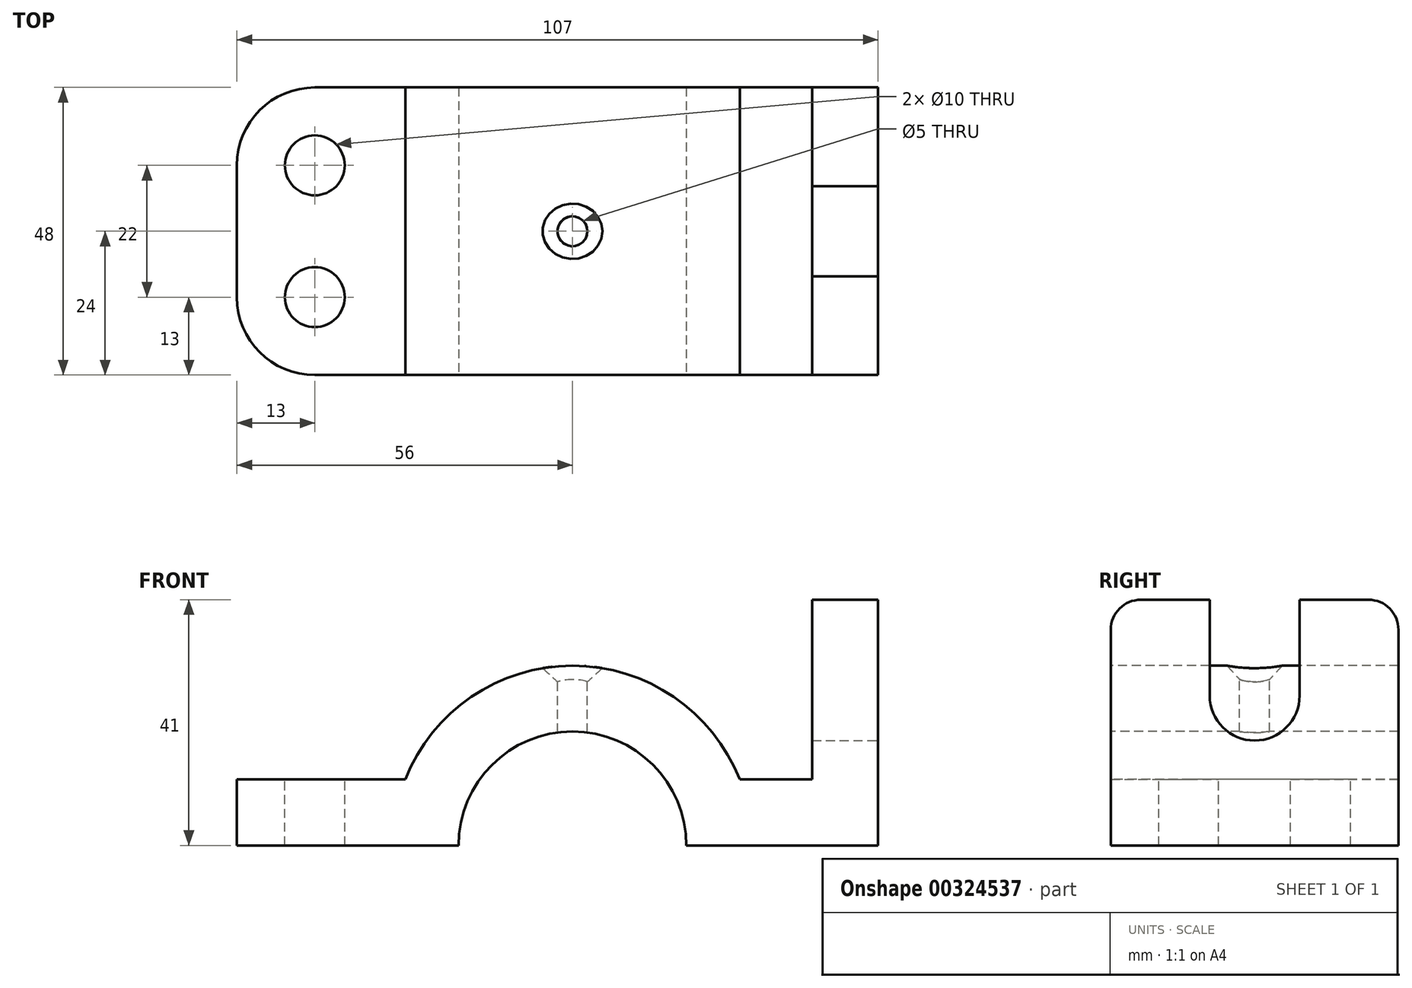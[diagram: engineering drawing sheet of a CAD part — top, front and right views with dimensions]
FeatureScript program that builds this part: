
annotation { "Feature Type Name" : "Feature", "Feature Type Description" : "" }
export const myFeature = defineFeature(function(context is Context, id is Id, definition is map)
    precondition{}
    {
        {
            var Q0;
            Q0=qCreatedBy(makeId("Top.planeOp"),FACE);
            var sketch = newSketch(context, id + "F0", { "sketchPlane" : qUnion([Q0])});
            skLineSegment(sketch, "E0", {"start": v(0, 0) * mm, "end": v(0, -48) * mm});
            skLineSegment(sketch, "E1", {"start": v(0, -48) * mm, "end": v(-11, -48) * mm});
            skLineSegment(sketch, "E2", {"start": v(-11, -48) * mm, "end": v(-11, 0) * mm});
            skLineSegment(sketch, "E3", {"start": v(-11, 0) * mm, "end": v(0, 0) * mm});
            skSolve(sketch);
        }
        {
            var Q0;
            Q0=makeQuery(id+"F0.imprint","IMPRINT",FACE,{"disambiguationData":[TD([[makeQuery(id+"F0.imprint","IMPRINT",EDGE,{"derivedFrom":sQuery(id+"F0.wireOp",EDGE,"E0")}),-1.0]])]});
            extrude(context, id + "F1", {"entities" : qUnion([Q0]), "depth" : 41 * mm});
        }
        {
            var Q0;
            Q0=makeQuery(id+"F1.opExtrude","CAP_EDGE",EDGE,{"disambiguationData":[OSD([sQuery(id+"F0.wireOp",EDGE,"E1")])],"isStart":false});
            var Q1;
            Q1=makeQuery(id+"F1.opExtrude","CAP_EDGE",EDGE,{"disambiguationData":[OSD([sQuery(id+"F0.wireOp",EDGE,"E3")])],"isStart":false});
            fillet(context, id + "F2", {"entities" : qUnion([Q0, Q1]), "radius" : 5 * mm, "tangentPropagation" : true, "allowEdgeOverflow" : false});
        }
        {
            var Q0;
            Q0=makeQuery(id+"F1.opExtrude","SWEPT_FACE",FACE,{"disambiguationData":[OSD([sQuery(id+"F0.wireOp",EDGE,"E0")])]});
            var sketch = newSketch(context, id + "F3", { "sketchPlane" : qUnion([Q0])});
            skLineSegment(sketch, "E4", {"start": v(-24, 41) * mm, "end": v(-24, 25) * mm});
            skPoint(sketch, "E4.endSnap0", {"position": v(-24, 41) * mm});
            skLineSegment(sketch, "E5", {"start": v(-24, 41) * mm, "end": v(-31.5, 41) * mm});
            skLineSegment(sketch, "E6", {"start": v(-24, 41) * mm, "end": v(-16.5, 41) * mm});
            skLineSegment(sketch, "E7", {"start": v(-31.5, 41) * mm, "end": v(-31.5, 25) * mm});
            skLineSegment(sketch, "E8", {"start": v(-16.5, 41) * mm, "end": v(-16.5, 25) * mm});
            skArc(sketch, "E9", {"start": v(-31.5, 25) * mm, "mid": v(-24, 17.5) * mm, "end": v(-16.5, 25) * mm});
            skSolve(sketch);
        }
        {
            var Q0;
            Q0=makeQuery(id+"F3.imprint","IMPRINT",FACE,{"disambiguationData":[TD([[makeQuery(id+"F3.imprint","IMPRINT",EDGE,{"derivedFrom":sQuery(id+"F3.wireOp",EDGE,"E5")}),1.0]])]});
            extrude(context, id + "F4", {"entities" : qUnion([Q0]), "operationType" : NewBodyOperationType.REMOVE, "oppositeDirection" : true, "depth" : 11 * mm});
        }
        {
            var Q0;
            Q0=makeQuery(id+"F1.opExtrude","SWEPT_FACE",FACE,{"disambiguationData":[OSD([sQuery(id+"F0.wireOp",EDGE,"E1")])]});
            var sketch = newSketch(context, id + "F5", { "sketchPlane" : qUnion([Q0])});
            skLineSegment(sketch, "E10", {"start": v(-107, 0) * mm, "end": v(-107, 11) * mm});
            skLineSegment(sketch, "E11", {"start": v(-11, 0) * mm, "end": v(-11, 11) * mm});
            skLineSegment(sketch, "E12", {"start": v(-107, 0) * mm, "end": v(-70, 0) * mm});
            skPoint(sketch, "E13", {"position": v(-51, 0) * mm});
            skArc(sketch, "E14", {"start": v(-32, 0) * mm, "mid": v(-51, 19) * mm, "end": v(-70, 0) * mm});
            skArc(sketch, "E15", {"start": v(-23.09, 11) * mm, "mid": v(-51, 30) * mm, "end": v(-78.91, 11) * mm});
            skLineSegment(sketch, "E16", {"start": v(-107, 11) * mm, "end": v(-78.91, 11) * mm});
            skLineSegment(sketch, "E17", {"start": v(-11, 11) * mm, "end": v(-23.09, 11) * mm});
            skLineSegment(sketch, "E18.trimOffspring", {"start": v(-32, 0) * mm, "end": v(0, 0) * mm});
            skSolve(sketch);
        }
        {
            var Q0;
            Q0=makeQuery(id+"F5.imprint","IMPRINT",FACE,{"disambiguationData":[TD([[makeQuery(id+"F5.imprint","IMPRINT",EDGE,{"derivedFrom":sQuery(id+"F5.wireOp",EDGE,"E10")}),-1.0]])]});
            extrude(context, id + "F6", {"entities" : qUnion([Q0]), "operationType" : NewBodyOperationType.ADD, "oppositeDirection" : true, "depth" : 48 * mm});
        }
        {
            var Q0;
            Q0=makeQuery(id+"F6.opExtrude","CAP_EDGE",EDGE,{"disambiguationData":[OSD([sQuery(id+"F5.wireOp",EDGE,"E10")])],"isStart":true});
            var Q1;
            Q1=makeQuery(id+"F6.opExtrude","CAP_EDGE",EDGE,{"disambiguationData":[OSD([sQuery(id+"F5.wireOp",EDGE,"E10")])],"isStart":false});
            fillet(context, id + "F7", {"entities" : qUnion([Q0, Q1]), "radius" : 13 * mm, "tangentPropagation" : true, "allowEdgeOverflow" : false});
        }
        {
            var Q0;
            Q0=makeQuery(id+"F6.opExtrude","SWEPT_FACE",FACE,{"disambiguationData":[OSD([sQuery(id+"F5.wireOp",EDGE,"E16")])]});
            var sketch = newSketch(context, id + "F8", { "sketchPlane" : qUnion([Q0])});
            skCircle(sketch, "E19", {"center": v(-94, -35) * mm, "radius": 5 * mm});
            skCircle(sketch, "E20", {"center": v(-94, -13) * mm, "radius": 5 * mm});
            skSolve(sketch);
        }
        {
            var Q0;
            Q0=makeQuery(id+"F8.imprint","IMPRINT",FACE,{"disambiguationData":[TD([[makeQuery(id+"F8.imprint","IMPRINT",EDGE,{"derivedFrom":sQuery(id+"F8.wireOp",EDGE,"E20")}),1.0]])]});
            var Q1;
            Q1=makeQuery(id+"F8.imprint","IMPRINT",FACE,{"disambiguationData":[TD([[makeQuery(id+"F8.imprint","IMPRINT",EDGE,{"derivedFrom":sQuery(id+"F8.wireOp",EDGE,"E19")}),1.0]])]});
            extrude(context, id + "F9", {"entities" : qUnion([Q0, Q1]), "operationType" : NewBodyOperationType.REMOVE, "endBound" : BoundingType.THROUGH_ALL, "oppositeDirection" : true, "depth" : 25 * mm});
        }
        {
            var Q0;
            Q0=qCreatedBy(makeId("Top.planeOp"),FACE);
            cPlane(context, id + "F10", {"entities" : qUnion([Q0]), "cplaneType" : CPlaneType.OFFSET, "offset" : 30 * mm, "width" : 150 * mm, "height" : 150 * mm});
        }
        {
            var Q0;
            Q0=qCreatedBy(id+"F10.planeOp",FACE);
            var sketch = newSketch(context, id + "F11", { "sketchPlane" : qUnion([Q0])});
            skCircle(sketch, "E21", {"center": v(-51, -24) * mm, "radius": 2.5 * mm});
            skSolve(sketch);
        }
        {
            var Q0;
            Q0=makeQuery(id+"F11.imprint","IMPRINT",FACE,{"disambiguationData":[TD([[makeQuery(id+"F11.imprint","IMPRINT",EDGE,{"derivedFrom":sQuery(id+"F11.wireOp",EDGE,"E21")}),1.0]])]});
            extrude(context, id + "F12", {"entities" : qUnion([Q0]), "operationType" : NewBodyOperationType.REMOVE, "endBound" : BoundingType.THROUGH_ALL, "oppositeDirection" : true, "depth" : 25 * mm});
        }
        {
            var Q0;
            Q0=makeQuery(id+"F12.boolean.opBoolean","INTERSECT",EDGE,{"derivedFrom":[makeQuery(id+"F6.opExtrude","SWEPT_FACE",FACE,{"disambiguationData":[OSD([sQuery(id+"F5.wireOp",EDGE,"E15")])]}),makeQuery(id+"F12.opExtrude","SWEPT_FACE",FACE,{"disambiguationData":[OSD([sQuery(id+"F11.wireOp",EDGE,"E21")])]})]});
            chamfer(context, id + "F13", {"entities" : qUnion([Q0]), "chamferType" : ChamferType.OFFSET_ANGLE, "width" : 2.5 * mm, "oppositeDirection" : false, "angle" : 45 * degree, "tangentPropagation" : true});
        }
    });
